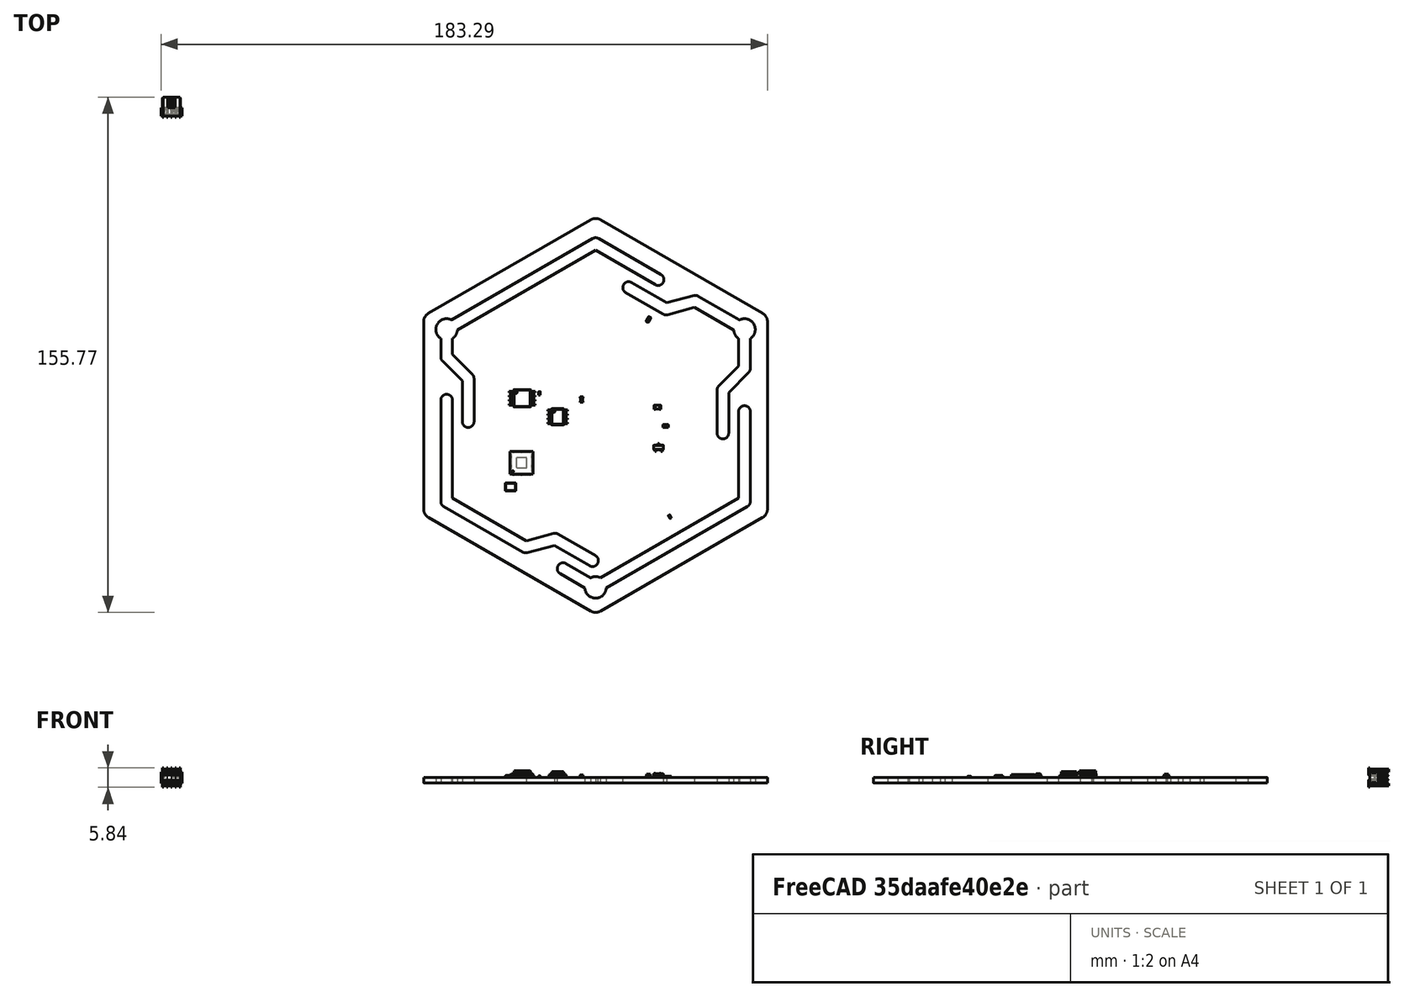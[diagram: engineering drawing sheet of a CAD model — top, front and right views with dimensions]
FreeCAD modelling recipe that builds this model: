
FCSTD DOCUMENT  (FreeCAD 0.21R33771 (Git))
Label: 3d_model
License: All rights reserved
LicenseURL: http://en.wikipedia.org/wiki/All_rights_reserved
objects: App::Link×38, Part::Feature×23, App::Part×5, PartDesign::CoordinateSystem×1, Sketcher::SketchObject×1
note: 25 computed .brp shape members not serialized (recipe doc carries the construction recipe); baked Part::Feature solids carry a one-line shape summary decoded from their .brp

FEATURE [PartDesign::CoordinateSystem] Local_CS_31ac
  AttacherType = Attacher::AttachEngine3D
  MapMode = 2
  Support = -> [X_Axis001]
FEATURE [Part::Feature] Pcb_31ac
  shape: bbox 103.9 x 119.2 x 1.6 mm, 89 faces (baked)
FEATURE [Sketcher::SketchObject] PCB_Sketch_31ac
  FullyConstrained = false
  sketch-geometry (357):
    g0: LineSegment StartX=171.398 StartY=-75.5717 StartZ=0 EndX=171.398 EndY=-67.2627 EndZ=0
    g1: LineSegment StartX=84.9254 StartY=-67.2627 StartZ=0 EndX=84.9254 EndY=-72.117 EndZ=0
    g2: LineSegment StartX=116.846 StartY=-126.377 StartZ=0 EndX=128.134 EndY=-132.894 EndZ=0
    g3: LineSegment StartX=81.3976 StartY=-116.498 StartZ=0 EndX=81.3976 EndY=-85.8817 EndZ=0
    g4: LineSegment StartX=168.408 StartY=-83.55 StartZ=0 EndX=168.408 EndY=-95.8535 EndZ=0
    g5: LineSegment StartX=165.397 StartY=-81.5722 StartZ=0 EndX=171.398 EndY=-75.5717 EndZ=0
    g6: LineSegment StartX=174.925 StartY=-89.3365 StartZ=0 EndX=174.925 EndY=-116.498 EndZ=0
    g7: LineSegment StartX=107.31 StartY=-128.404 StartZ=0 EndX=115.506 EndY=-126.201 EndZ=0
    g8: LineSegment StartX=178.623 StartY=-121.384 StartZ=0 EndX=129.662 EndY=-149.652 EndZ=0
    g9: LineSegment StartX=106.179 StartY=-131.825 StartZ=0 EndX=82.2796 EndY=-118.026 EndZ=0
    g10: LineSegment StartX=129.662 StartY=-31.3837 StartZ=0 EndX=178.623 EndY=-59.6516 EndZ=0
    g11: LineSegment StartX=174.925 StartY=-67.2627 StartZ=0 EndX=174.925 EndY=-76.3024 EndZ=0
    g12: LineSegment StartX=124.916 StartY=-142.642 StartZ=0 EndX=117.467 EndY=-138.342 EndZ=0
    g13: LineSegment StartX=84.6472 StartY=-61.6424 StartZ=0 EndX=127.28 EndY=-37.0286 EndZ=0
    g14: LineSegment StartX=84.9254 StartY=-85.8817 StartZ=0 EndX=84.9254 EndY=-115.48 EndZ=0
    g15: LineSegment StartX=84.9254 StartY=-72.117 StartZ=0 EndX=90.9258 EndY=-78.1174 EndZ=0
    g16: LineSegment StartX=149.694 StartY=-56.4882 StartZ=0 EndX=157.891 EndY=-54.2919 EndZ=0
    g17: LineSegment StartX=139.039 StartY=-50.3365 StartZ=0 EndX=149.694 EndY=-56.4882 EndZ=0
    g18: LineSegment StartX=148.563 StartY=-59.9087 StartZ=0 EndX=137.275 EndY=-53.3916 EndZ=0
    g19: LineSegment StartX=77.6829 StartY=-59.6615 StartZ=0 EndX=126.662 EndY=-31.3837 EndZ=0
    g20: LineSegment StartX=126.37 StartY=-135.949 StartZ=0 EndX=115.715 EndY=-129.798 EndZ=0
    g21: LineSegment StartX=128.161 StartY=-40.5932 StartZ=0 EndX=86.4073 EndY=-64.6997 EndZ=0
    g22: LineSegment StartX=159.229 StartY=-54.4676 StartZ=0 EndX=171.674 EndY=-61.6432 EndZ=0
    g23: LineSegment StartX=81.3976 StartY=-72.8476 StartZ=0 EndX=81.3976 EndY=-67.2627 EndZ=0
    g24: LineSegment StartX=146.177 StartY=-51.0058 StartZ=0 EndX=128.161 EndY=-40.5932 EndZ=0
    g25: LineSegment StartX=171.398 StartY=-115.48 StartZ=0 EndX=171.398 EndY=-89.3365 EndZ=0
    g26: LineSegment StartX=174.043 StartY=-118.026 StartZ=0 EndX=131.408 EndY=-142.642 EndZ=0
    g27: LineSegment StartX=119.231 StartY=-135.286 StartZ=0 EndX=126.679 EndY=-139.587 EndZ=0
    g28: LineSegment StartX=129.644 StartY=-139.587 StartZ=0 EndX=171.398 EndY=-115.48 EndZ=0
    g29: LineSegment StartX=115.715 StartY=-129.798 StartZ=0 EndX=107.519 EndY=-132 EndZ=0
    g30: LineSegment StartX=91.4425 StartY=-79.3646 StartZ=0 EndX=91.4425 EndY=-92.3987 EndZ=0
    g31: LineSegment StartX=76.2 StartY=-118.8 StartZ=0 EndX=76.2 EndY=-62.23 EndZ=0
    g32: LineSegment StartX=84.9254 StartY=-115.48 StartZ=0 EndX=107.31 EndY=-128.404 EndZ=0
    g33: LineSegment StartX=164.881 StartY=-95.8535 StartZ=0 EndX=164.881 EndY=-82.8194 EndZ=0
    g34: LineSegment StartX=129.044 StartY=-37.029 StartZ=0 EndX=147.942 EndY=-47.9515 EndZ=0
    g35: LineSegment StartX=158.099 StartY=-57.8884 StartZ=0 EndX=149.902 EndY=-60.0849 EndZ=0
    g36: LineSegment StartX=169.916 StartY=-64.7016 StartZ=0 EndX=158.099 EndY=-57.8884 EndZ=0
    g37: LineSegment StartX=174.409 StartY=-77.5496 StartZ=0 EndX=168.408 EndY=-83.55 EndZ=0
    g38: LineSegment StartX=87.9147 StartY=-80.0953 StartZ=0 EndX=81.9143 EndY=-74.0949 EndZ=0
    g39: LineSegment StartX=180.123 StartY=-62.2497 StartZ=0 EndX=180.123 EndY=-118.786 EndZ=0
    g40: LineSegment StartX=87.9147 StartY=-92.3987 StartZ=0 EndX=87.9147 EndY=-80.0953 EndZ=0
    g41: LineSegment StartX=126.662 StartY=-149.652 StartZ=0 EndX=77.6877 EndY=-121.377 EndZ=0
    g42: BSplineCurve PolesCount=4 KnotsCount=2 Degree=3 IsPeriodic=0
    g43: BSplineCurve PolesCount=4 KnotsCount=2 Degree=3 IsPeriodic=0
    g44: BSplineCurve PolesCount=4 KnotsCount=2 Degree=3 IsPeriodic=0
    g45: BSplineCurve PolesCount=4 KnotsCount=2 Degree=3 IsPeriodic=0
    g46: BSplineCurve PolesCount=4 KnotsCount=2 Degree=3 IsPeriodic=0
    g47: BSplineCurve PolesCount=4 KnotsCount=2 Degree=3 IsPeriodic=0
    g48: BSplineCurve PolesCount=4 KnotsCount=2 Degree=3 IsPeriodic=0
    g49: BSplineCurve PolesCount=4 KnotsCount=2 Degree=3 IsPeriodic=0
    g50: BSplineCurve PolesCount=4 KnotsCount=2 Degree=3 IsPeriodic=0
    g51: BSplineCurve PolesCount=4 KnotsCount=2 Degree=3 IsPeriodic=0
    g52: BSplineCurve PolesCount=4 KnotsCount=2 Degree=3 IsPeriodic=0
    g53: BSplineCurve PolesCount=4 KnotsCount=2 Degree=3 IsPeriodic=0
    g54: BSplineCurve PolesCount=4 KnotsCount=2 Degree=3 IsPeriodic=0
    g55: BSplineCurve PolesCount=4 KnotsCount=2 Degree=3 IsPeriodic=0
    g56: BSplineCurve PolesCount=4 KnotsCount=2 Degree=3 IsPeriodic=0
    g57: BSplineCurve PolesCount=4 KnotsCount=2 Degree=3 IsPeriodic=0
    g58: BSplineCurve PolesCount=4 KnotsCount=2 Degree=3 IsPeriodic=0
    g59: BSplineCurve PolesCount=4 KnotsCount=2 Degree=3 IsPeriodic=0
    g60: BSplineCurve PolesCount=4 KnotsCount=2 Degree=3 IsPeriodic=0
    g61: BSplineCurve PolesCount=4 KnotsCount=2 Degree=3 IsPeriodic=0
    g62: BSplineCurve PolesCount=4 KnotsCount=2 Degree=3 IsPeriodic=0
    g63: BSplineCurve PolesCount=4 KnotsCount=2 Degree=3 IsPeriodic=0
    g64: BSplineCurve PolesCount=4 KnotsCount=2 Degree=3 IsPeriodic=0
    g65: BSplineCurve PolesCount=4 KnotsCount=2 Degree=3 IsPeriodic=0
    g66: BSplineCurve PolesCount=4 KnotsCount=2 Degree=3 IsPeriodic=0
    g67: BSplineCurve PolesCount=4 KnotsCount=2 Degree=3 IsPeriodic=0
    g68: BSplineCurve PolesCount=4 KnotsCount=2 Degree=3 IsPeriodic=0
    g69: BSplineCurve PolesCount=4 KnotsCount=2 Degree=3 IsPeriodic=0
    g70: BSplineCurve PolesCount=4 KnotsCount=2 Degree=3 IsPeriodic=0
    g71: BSplineCurve PolesCount=4 KnotsCount=2 Degree=3 IsPeriodic=0
    g72: BSplineCurve PolesCount=4 KnotsCount=2 Degree=3 IsPeriodic=0
    g73: BSplineCurve PolesCount=4 KnotsCount=2 Degree=3 IsPeriodic=0
    g74: BSplineCurve PolesCount=4 KnotsCount=2 Degree=3 IsPeriodic=0
    g75: BSplineCurve PolesCount=4 KnotsCount=2 Degree=3 IsPeriodic=0
    g76: BSplineCurve PolesCount=4 KnotsCount=2 Degree=3 IsPeriodic=0
    g77: BSplineCurve PolesCount=4 KnotsCount=2 Degree=3 IsPeriodic=0
    g78: BSplineCurve PolesCount=4 KnotsCount=2 Degree=3 IsPeriodic=0
    g79: BSplineCurve PolesCount=4 KnotsCount=2 Degree=3 IsPeriodic=0
    g80: BSplineCurve PolesCount=4 KnotsCount=2 Degree=3 IsPeriodic=0
    g81: BSplineCurve PolesCount=4 KnotsCount=2 Degree=3 IsPeriodic=0
    g82: BSplineCurve PolesCount=4 KnotsCount=2 Degree=3 IsPeriodic=0
    g83: BSplineCurve PolesCount=4 KnotsCount=2 Degree=3 IsPeriodic=0
    g84: BSplineCurve PolesCount=4 KnotsCount=2 Degree=3 IsPeriodic=0
    g85: BSplineCurve PolesCount=4 KnotsCount=2 Degree=3 IsPeriodic=0
    g86: BSplineCurve PolesCount=4 KnotsCount=2 Degree=3 IsPeriodic=0
    g87-g90: Circle x4 (B-spline internal-alignment scaffolding for g42; pole/knot coordinates omitted)
    g91: GeomPoint X=126.662 Y=-31.3837 Z=0
    g92: GeomPoint X=129.662 Y=-31.3837 Z=0
    g93-g96: Circle x4 (B-spline internal-alignment scaffolding for g43; pole/knot coordinates omitted)
    g97: GeomPoint X=157.891 Y=-54.2919 Z=0
    g98: GeomPoint X=159.229 Y=-54.4676 Z=0
    g99-g102: Circle x4 (B-spline internal-alignment scaffolding for g44; pole/knot coordinates omitted)
    g103: GeomPoint X=147.942 Y=-47.9515 Z=0
    g104: GeomPoint X=148.587 Y=-50.3613 Z=0
    g105-g108: Circle x4 (B-spline internal-alignment scaffolding for g45; pole/knot coordinates omitted)
    g109: GeomPoint X=83.1615 Y=-61.2831 Z=0
    g110: GeomPoint X=84.6472 Y=-61.6424 Z=0
    g111-g114: Circle x4 (B-spline internal-alignment scaffolding for g46; pole/knot coordinates omitted)
    g115: GeomPoint X=81.3976 Y=-67.2627 Z=0
    g116: GeomPoint X=79.9115 Y=-64.5332 Z=0
    g117-g120: Circle x4 (B-spline internal-alignment scaffolding for g47; pole/knot coordinates omitted)
    g121: GeomPoint X=131.408 Y=-142.642 Z=0
    g122: GeomPoint X=128.162 Y=-145.729 Z=0
    g123-g126: Circle x4 (B-spline internal-alignment scaffolding for g48; pole/knot coordinates omitted)
    g127: GeomPoint X=90.9258 Y=-78.1174 Z=0
    g128: GeomPoint X=91.4425 Y=-79.3646 Z=0
    g129-g132: Circle x4 (B-spline internal-alignment scaffolding for g49; pole/knot coordinates omitted)
    g133: GeomPoint X=176.412 Y=-64.5332 Z=0
    g134: GeomPoint X=174.925 Y=-67.2627 Z=0
    g135-g138: Circle x4 (B-spline internal-alignment scaffolding for g50; pole/knot coordinates omitted)
    g139: GeomPoint X=180.123 Y=-118.786 Z=0
    g140: GeomPoint X=178.623 Y=-121.384 Z=0
    g141-g144: Circle x4 (B-spline internal-alignment scaffolding for g51; pole/knot coordinates omitted)
    g145: GeomPoint X=164.881 Y=-82.8194 Z=0
    g146: GeomPoint X=165.397 Y=-81.5722 Z=0
    g147-g150: Circle x4 (B-spline internal-alignment scaffolding for g52; pole/knot coordinates omitted)
    g151: GeomPoint X=117.467 Y=-138.342 Z=0
    g152: GeomPoint X=116.822 Y=-135.932 Z=0
    g153-g156: Circle x4 (B-spline internal-alignment scaffolding for g53; pole/knot coordinates omitted)
    g157: GeomPoint X=81.3976 Y=-85.8817 Z=0
    g158: GeomPoint X=83.1615 Y=-84.1178 Z=0
    g159-g162: Circle x4 (B-spline internal-alignment scaffolding for g54; pole/knot coordinates omitted)
    g163: GeomPoint X=126.679 Y=-139.587 Z=0
    g164: GeomPoint X=128.162 Y=-139.229 Z=0
    g165-g168: Circle x4 (B-spline internal-alignment scaffolding for g55; pole/knot coordinates omitted)
    g169: GeomPoint X=107.519 Y=-132 Z=0
    g170: GeomPoint X=106.179 Y=-131.825 Z=0
    g171-g174: Circle x4 (B-spline internal-alignment scaffolding for g56; pole/knot coordinates omitted)
    g175: GeomPoint X=115.506 Y=-126.201 Z=0
    g176: GeomPoint X=116.846 Y=-126.377 Z=0
    g177-g180: Circle x4 (B-spline internal-alignment scaffolding for g57; pole/knot coordinates omitted)
    g181: GeomPoint X=137.275 Y=-53.3916 Z=0
    g182: GeomPoint X=136.63 Y=-50.9821 Z=0
    g183-g186: Circle x4 (B-spline internal-alignment scaffolding for g58; pole/knot coordinates omitted)
    g187: GeomPoint X=76.2 Y=-62.23 Z=0
    g188: GeomPoint X=77.6829 Y=-59.6615 Z=0
    g189-g192: Circle x4 (B-spline internal-alignment scaffolding for g59; pole/knot coordinates omitted)
    g193: GeomPoint X=128.134 Y=-132.894 Z=0
    g194: GeomPoint X=128.779 Y=-135.303 Z=0
    g195-g198: Circle x4 (B-spline internal-alignment scaffolding for g60; pole/knot coordinates omitted)
    g199: GeomPoint X=136.63 Y=-50.9821 Z=0
    g200: GeomPoint X=139.039 Y=-50.3365 Z=0
    g201-g204: Circle x4 (B-spline internal-alignment scaffolding for g61; pole/knot coordinates omitted)
    g205: GeomPoint X=127.28 Y=-37.0286 Z=0
    g206: GeomPoint X=129.044 Y=-37.029 Z=0
    g207-g210: Circle x4 (B-spline internal-alignment scaffolding for g62; pole/knot coordinates omitted)
    g211: GeomPoint X=128.162 Y=-145.729 Z=0
    g212: GeomPoint X=124.916 Y=-142.642 Z=0
    g213-g216: Circle x4 (B-spline internal-alignment scaffolding for g63; pole/knot coordinates omitted)
    g217: GeomPoint X=79.9115 Y=-64.5332 Z=0
    g218: GeomPoint X=83.1615 Y=-61.2831 Z=0
    g219-g222: Circle x4 (B-spline internal-alignment scaffolding for g64; pole/knot coordinates omitted)
    g223: GeomPoint X=174.925 Y=-116.498 Z=0
    g224: GeomPoint X=174.043 Y=-118.026 Z=0
    g225-g228: Circle x4 (B-spline internal-alignment scaffolding for g65; pole/knot coordinates omitted)
    g229: GeomPoint X=116.822 Y=-135.932 Z=0
    g230: GeomPoint X=119.231 Y=-135.286 Z=0
    g231-g234: Circle x4 (B-spline internal-alignment scaffolding for g66; pole/knot coordinates omitted)
    g235: GeomPoint X=82.2796 Y=-118.026 Z=0
    g236: GeomPoint X=81.3976 Y=-116.498 Z=0
    g237-g240: Circle x4 (B-spline internal-alignment scaffolding for g67; pole/knot coordinates omitted)
    g241: GeomPoint X=168.408 Y=-95.8535 Z=0
    g242: GeomPoint X=166.644 Y=-97.6174 Z=0
    g243-g246: Circle x4 (B-spline internal-alignment scaffolding for g68; pole/knot coordinates omitted)
    g247: GeomPoint X=148.587 Y=-50.3613 Z=0
    g248: GeomPoint X=146.177 Y=-51.0058 Z=0
    g249-g252: Circle x4 (B-spline internal-alignment scaffolding for g69; pole/knot coordinates omitted)
    g253: GeomPoint X=171.674 Y=-61.6432 Z=0
    g254: GeomPoint X=173.162 Y=-61.2831 Z=0
    g255-g258: Circle x4 (B-spline internal-alignment scaffolding for g70; pole/knot coordinates omitted)
    g259: GeomPoint X=128.779 Y=-135.303 Z=0
    g260: GeomPoint X=126.37 Y=-135.949 Z=0
    g261-g264: Circle x4 (B-spline internal-alignment scaffolding for g71; pole/knot coordinates omitted)
    g265: GeomPoint X=81.9143 Y=-74.0949 Z=0
    g266: GeomPoint X=81.3976 Y=-72.8476 Z=0
    g267-g270: Circle x4 (B-spline internal-alignment scaffolding for g72; pole/knot coordinates omitted)
    g271: GeomPoint X=171.398 Y=-89.3365 Z=0
    g272: GeomPoint X=173.162 Y=-87.5726 Z=0
    g273-g276: Circle x4 (B-spline internal-alignment scaffolding for g73; pole/knot coordinates omitted)
    g277: GeomPoint X=129.662 Y=-149.652 Z=0
    g278: GeomPoint X=126.662 Y=-149.652 Z=0
    g279-g282: Circle x4 (B-spline internal-alignment scaffolding for g74; pole/knot coordinates omitted)
    g283: GeomPoint X=77.6877 Y=-121.377 Z=0
    g284: GeomPoint X=76.2 Y=-118.8 Z=0
    g285-g288: Circle x4 (B-spline internal-alignment scaffolding for g75; pole/knot coordinates omitted)
    g289: GeomPoint X=86.4073 Y=-64.6997 Z=0
    g290: GeomPoint X=84.9254 Y=-67.2627 Z=0
    g291-g294: Circle x4 (B-spline internal-alignment scaffolding for g76; pole/knot coordinates omitted)
    g295: GeomPoint X=91.4425 Y=-92.3987 Z=0
    g296: GeomPoint X=89.6786 Y=-94.1626 Z=0
    g297-g300: Circle x4 (B-spline internal-alignment scaffolding for g77; pole/knot coordinates omitted)
    g301: GeomPoint X=171.398 Y=-67.2627 Z=0
    g302: GeomPoint X=169.916 Y=-64.7016 Z=0
    g303-g306: Circle x4 (B-spline internal-alignment scaffolding for g78; pole/knot coordinates omitted)
    g307: GeomPoint X=173.162 Y=-61.2831 Z=0
    g308: GeomPoint X=176.412 Y=-64.5332 Z=0
    g309-g312: Circle x4 (B-spline internal-alignment scaffolding for g79; pole/knot coordinates omitted)
    g313: GeomPoint X=89.6786 Y=-94.1626 Z=0
    g314: GeomPoint X=87.9147 Y=-92.3987 Z=0
    g315-g318: Circle x4 (B-spline internal-alignment scaffolding for g80; pole/knot coordinates omitted)
    g319: GeomPoint X=149.902 Y=-60.0849 Z=0
    g320: GeomPoint X=148.563 Y=-59.9087 Z=0
    g321-g324: Circle x4 (B-spline internal-alignment scaffolding for g81; pole/knot coordinates omitted)
    g325: GeomPoint X=128.162 Y=-139.229 Z=0
    g326: GeomPoint X=129.644 Y=-139.587 Z=0
    g327-g330: Circle x4 (B-spline internal-alignment scaffolding for g82; pole/knot coordinates omitted)
    g331: GeomPoint X=166.644 Y=-97.6174 Z=0
    g332: GeomPoint X=164.881 Y=-95.8535 Z=0
    g333-g336: Circle x4 (B-spline internal-alignment scaffolding for g83; pole/knot coordinates omitted)
    g337: GeomPoint X=178.623 Y=-59.6516 Z=0
    g338: GeomPoint X=180.123 Y=-62.2497 Z=0
    g339-g342: Circle x4 (B-spline internal-alignment scaffolding for g84; pole/knot coordinates omitted)
    g343: GeomPoint X=173.162 Y=-87.5726 Z=0
    g344: GeomPoint X=174.925 Y=-89.3365 Z=0
    g345-g348: Circle x4 (B-spline internal-alignment scaffolding for g85; pole/knot coordinates omitted)
    g349: GeomPoint X=83.1615 Y=-84.1178 Z=0
    g350: GeomPoint X=84.9254 Y=-85.8817 Z=0
    g351-g354: Circle x4 (B-spline internal-alignment scaffolding for g86; pole/knot coordinates omitted)
    g355: GeomPoint X=174.925 Y=-76.3024 Z=0
    g356: GeomPoint X=174.409 Y=-77.5496 Z=0
  constraints (537):
    c: Coincident(g31,g74)
    c: Coincident(g31,g58)
    c: Coincident(g41,g74)
    c: Coincident(g19,g58)
    c: Coincident(g46,g63)
    c: Coincident(g3,g66)
    c: Coincident(g3,g53)
    c: Coincident(g23,g71)
    c: Coincident(g23,g46)
    c: Coincident(g38,g71)
    c: Coincident(g9,g66)
    c: Coincident(g53,g85)
    c: Coincident(g45,g63)
    c: Coincident(g13,g45)
    c: Coincident(g14,g32)
    c: Coincident(g14,g85)
    c: Coincident(g1,g15)
    c: Coincident(g1,g75)
    c: Coincident(g21,g75)
    c: Coincident(g40,g79)
    c: Coincident(g38,g40)
    c: Coincident(g76,g79)
    c: Coincident(g15,g48)
    c: Coincident(g30,g76)
    c: Coincident(g30,g48)
    c: Coincident(g9,g55)
    c: Coincident(g7,g32)
    c: Coincident(g29,g55)
    c: Coincident(g7,g56)
    c: Coincident(g20,g29)
    c: Coincident(g52,g65)
    c: Coincident(g2,g56)
    c: Coincident(g12,g52)
    c: Coincident(g27,g65)
    c: Coincident(g12,g62)
    c: Coincident(g20,g70)
    c: Coincident(g41,g73)
    c: Coincident(g19,g42)
    c: Coincident(g27,g54)
    c: Coincident(g13,g61)
    c: Coincident(g2,g59)
    c: Coincident(g47,g62)
    c: Coincident(g54,g81)
    c: Coincident(g21,g24)
    c: Coincident(g59,g70)
    c: Coincident(g34,g61)
    c: Coincident(g28,g81)
    c: Coincident(g8,g73)
    c: Coincident(g10,g42)
    c: Coincident(g26,g47)
    c: Coincident(g57,g60)
    c: Coincident(g18,g57)
    c: Coincident(g17,g60)
    c: Coincident(g24,g68)
    c: Coincident(g34,g44)
    c: Coincident(g18,g80)
    c: Coincident(g44,g68)
    c: Coincident(g16,g17)
    c: Coincident(g35,g80)
    c: Coincident(g16,g43)
    c: Coincident(g35,g36)
    c: Coincident(g22,g43)
    c: Coincident(g33,g82)
    c: Coincident(g33,g51)
    c: Coincident(g5,g51)
    c: Coincident(g67,g82)
    c: Coincident(g4,g67)
    c: Coincident(g4,g37)
    c: Coincident(g36,g77)
    c: Coincident(g25,g28)
    c: Coincident(g25,g72)
    c: Coincident(g0,g5)
    c: Coincident(g0,g77)
    c: Coincident(g22,g69)
    c: Coincident(g72,g84)
    c: Coincident(g69,g78)
    c: Coincident(g26,g64)
    c: Coincident(g37,g86)
    c: Coincident(g6,g64)
    c: Coincident(g6,g84)
    c: Coincident(g11,g86)
    c: Coincident(g11,g49)
    c: Coincident(g49,g78)
    c: Coincident(g8,g50)
    c: Coincident(g10,g83)
    c: Coincident(g39,g50)
    c: Coincident(g39,g83)
    c: InternalAlignment(g87,g42)
    c: Weight(g87) = 1
    c: InternalAlignment(g88,g42)
    c: Equal(g88,g87)
    c: InternalAlignment(g89,g42)
    c: Equal(g89,g87)
    c: InternalAlignment(g90,g42)
    c: Equal(g90,g87)
    c: InternalAlignment(g91,g42)
    c: InternalAlignment(g92,g42)
    c: InternalAlignment(g93,g43)
    c: Weight(g93) = 1
    c: InternalAlignment(g94,g43)
    c: Equal(g94,g93)
    c: InternalAlignment(g95,g43)
    c: Equal(g95,g93)
    c: InternalAlignment(g96,g43)
    c: Equal(g96,g93)
    c: InternalAlignment(g97,g43)
    c: InternalAlignment(g98,g43)
    c: InternalAlignment(g99,g44)
    c: Weight(g99) = 1
    c: InternalAlignment(g100,g44)
    c: Equal(g100,g99)
    c: InternalAlignment(g101,g44)
    c: Equal(g101,g99)
    c: InternalAlignment(g102,g44)
    c: Equal(g102,g99)
    c: InternalAlignment(g103,g44)
    c: InternalAlignment(g104,g44)
    c: InternalAlignment(g105,g45)
    c: Weight(g105) = 1
    c: InternalAlignment(g106,g45)
    c: Equal(g106,g105)
    c: InternalAlignment(g107,g45)
    c: Equal(g107,g105)
    c: InternalAlignment(g108,g45)
    c: Equal(g108,g105)
    c: InternalAlignment(g109,g45)
    c: InternalAlignment(g110,g45)
    c: InternalAlignment(g111,g46)
    c: Weight(g111) = 1
    c: InternalAlignment(g112,g46)
    c: Equal(g112,g111)
    c: InternalAlignment(g113,g46)
    c: Equal(g113,g111)
    c: InternalAlignment(g114,g46)
    c: Equal(g114,g111)
    c: InternalAlignment(g115,g46)
    c: InternalAlignment(g116,g46)
    c: InternalAlignment(g117,g47)
    c: Weight(g117) = 1
    c: InternalAlignment(g118,g47)
    c: Equal(g118,g117)
    c: InternalAlignment(g119,g47)
    c: Equal(g119,g117)
    c: InternalAlignment(g120,g47)
    c: Equal(g120,g117)
    c: InternalAlignment(g121,g47)
    c: InternalAlignment(g122,g47)
    c: InternalAlignment(g123,g48)
    c: Weight(g123) = 1
    c: InternalAlignment(g124,g48)
    c: Equal(g124,g123)
    c: InternalAlignment(g125,g48)
    c: Equal(g125,g123)
    c: InternalAlignment(g126,g48)
    c: Equal(g126,g123)
    c: InternalAlignment(g127,g48)
    c: InternalAlignment(g128,g48)
    c: InternalAlignment(g129,g49)
    c: Weight(g129) = 1
    c: InternalAlignment(g130,g49)
    c: Equal(g130,g129)
    c: InternalAlignment(g131,g49)
    c: Equal(g131,g129)
    c: InternalAlignment(g132,g49)
    c: Equal(g132,g129)
    c: InternalAlignment(g133,g49)
    c: InternalAlignment(g134,g49)
    c: InternalAlignment(g135,g50)
    c: Weight(g135) = 1
    c: InternalAlignment(g136,g50)
    c: Equal(g136,g135)
    c: InternalAlignment(g137,g50)
    c: Equal(g137,g135)
    c: InternalAlignment(g138,g50)
    c: Equal(g138,g135)
    c: InternalAlignment(g139,g50)
    c: InternalAlignment(g140,g50)
    c: InternalAlignment(g141,g51)
    c: Weight(g141) = 1
    c: InternalAlignment(g142,g51)
    c: Equal(g142,g141)
    c: InternalAlignment(g143,g51)
    c: Equal(g143,g141)
    c: InternalAlignment(g144,g51)
    c: Equal(g144,g141)
    c: InternalAlignment(g145,g51)
    c: InternalAlignment(g146,g51)
    c: InternalAlignment(g147,g52)
    c: Weight(g147) = 1
    c: InternalAlignment(g148,g52)
    c: Equal(g148,g147)
    c: InternalAlignment(g149,g52)
    c: Equal(g149,g147)
    c: InternalAlignment(g150,g52)
    c: Equal(g150,g147)
    c: InternalAlignment(g151,g52)
    c: InternalAlignment(g152,g52)
    c: InternalAlignment(g153,g53)
    c: Weight(g153) = 1
    c: InternalAlignment(g154,g53)
    c: Equal(g154,g153)
    c: InternalAlignment(g155,g53)
    c: Equal(g155,g153)
    c: InternalAlignment(g156,g53)
    c: Equal(g156,g153)
    c: InternalAlignment(g157,g53)
    c: InternalAlignment(g158,g53)
    c: InternalAlignment(g159,g54)
    c: Weight(g159) = 1
    c: InternalAlignment(g160,g54)
    c: Equal(g160,g159)
    c: InternalAlignment(g161,g54)
    c: Equal(g161,g159)
    c: InternalAlignment(g162,g54)
    c: Equal(g162,g159)
    c: InternalAlignment(g163,g54)
    c: InternalAlignment(g164,g54)
    c: InternalAlignment(g165,g55)
    c: Weight(g165) = 1
    c: InternalAlignment(g166,g55)
    c: Equal(g166,g165)
    c: InternalAlignment(g167,g55)
    c: Equal(g167,g165)
    c: InternalAlignment(g168,g55)
    c: Equal(g168,g165)
    c: InternalAlignment(g169,g55)
    c: InternalAlignment(g170,g55)
    c: InternalAlignment(g171,g56)
    c: Weight(g171) = 1
    c: InternalAlignment(g172,g56)
    c: Equal(g172,g171)
    c: InternalAlignment(g173,g56)
    c: Equal(g173,g171)
    c: InternalAlignment(g174,g56)
    c: Equal(g174,g171)
    c: InternalAlignment(g175,g56)
    c: InternalAlignment(g176,g56)
    c: InternalAlignment(g177,g57)
    c: Weight(g177) = 1
    c: InternalAlignment(g178,g57)
    c: Equal(g178,g177)
    c: InternalAlignment(g179,g57)
    c: Equal(g179,g177)
    c: InternalAlignment(g180,g57)
    c: Equal(g180,g177)
    c: InternalAlignment(g181,g57)
    c: InternalAlignment(g182,g57)
    c: InternalAlignment(g183,g58)
    c: Weight(g183) = 1
    c: InternalAlignment(g184,g58)
    c: Equal(g184,g183)
    c: InternalAlignment(g185,g58)
    c: Equal(g185,g183)
    c: InternalAlignment(g186,g58)
    c: Equal(g186,g183)
    c: InternalAlignment(g187,g58)
    c: InternalAlignment(g188,g58)
    c: InternalAlignment(g189,g59)
    c: Weight(g189) = 1
    c: InternalAlignment(g190,g59)
    c: Equal(g190,g189)
    c: InternalAlignment(g191,g59)
    c: Equal(g191,g189)
    c: InternalAlignment(g192,g59)
    c: Equal(g192,g189)
    c: InternalAlignment(g193,g59)
    c: InternalAlignment(g194,g59)
    c: InternalAlignment(g195,g60)
    c: Weight(g195) = 1
    c: InternalAlignment(g196,g60)
    c: Equal(g196,g195)
    c: InternalAlignment(g197,g60)
    c: Equal(g197,g195)
    c: InternalAlignment(g198,g60)
    c: Equal(g198,g195)
    c: InternalAlignment(g199,g60)
    c: InternalAlignment(g200,g60)
    c: InternalAlignment(g201,g61)
    c: Weight(g201) = 1
    c: InternalAlignment(g202,g61)
    c: Equal(g202,g201)
    c: InternalAlignment(g203,g61)
    c: Equal(g203,g201)
    c: InternalAlignment(g204,g61)
    c: Equal(g204,g201)
    c: InternalAlignment(g205,g61)
    c: InternalAlignment(g206,g61)
    c: InternalAlignment(g207,g62)
    c: Weight(g207) = 1
    c: InternalAlignment(g208,g62)
    c: Equal(g208,g207)
    c: InternalAlignment(g209,g62)
    c: Equal(g209,g207)
    c: InternalAlignment(g210,g62)
    c: Equal(g210,g207)
    c: InternalAlignment(g211,g62)
    c: InternalAlignment(g212,g62)
    c: InternalAlignment(g213,g63)
    c: Weight(g213) = 1
    c: InternalAlignment(g214,g63)
    c: Equal(g214,g213)
    c: InternalAlignment(g215,g63)
    c: Equal(g215,g213)
    c: InternalAlignment(g216,g63)
    c: Equal(g216,g213)
    c: InternalAlignment(g217,g63)
    c: InternalAlignment(g218,g63)
    c: InternalAlignment(g219,g64)
    c: Weight(g219) = 1
    c: InternalAlignment(g220,g64)
    c: Equal(g220,g219)
    c: InternalAlignment(g221,g64)
    c: Equal(g221,g219)
    c: InternalAlignment(g222,g64)
    c: Equal(g222,g219)
    c: InternalAlignment(g223,g64)
    c: InternalAlignment(g224,g64)
    c: InternalAlignment(g225,g65)
    c: Weight(g225) = 1
    c: InternalAlignment(g226,g65)
    c: Equal(g226,g225)
    c: InternalAlignment(g227,g65)
    c: Equal(g227,g225)
    c: InternalAlignment(g228,g65)
    c: Equal(g228,g225)
    c: InternalAlignment(g229,g65)
    c: InternalAlignment(g230,g65)
    c: InternalAlignment(g231,g66)
    c: Weight(g231) = 1
    c: InternalAlignment(g232,g66)
    c: Equal(g232,g231)
    c: InternalAlignment(g233,g66)
    c: Equal(g233,g231)
    c: InternalAlignment(g234,g66)
    c: Equal(g234,g231)
    c: InternalAlignment(g235,g66)
    c: InternalAlignment(g236,g66)
    c: InternalAlignment(g237,g67)
    c: Weight(g237) = 1
    c: InternalAlignment(g238,g67)
    c: Equal(g238,g237)
    c: InternalAlignment(g239,g67)
    c: Equal(g239,g237)
    c: InternalAlignment(g240,g67)
    c: Equal(g240,g237)
    c: InternalAlignment(g241,g67)
    c: InternalAlignment(g242,g67)
    c: InternalAlignment(g243,g68)
    c: Weight(g243) = 1
    c: InternalAlignment(g244,g68)
    c: Equal(g244,g243)
    c: InternalAlignment(g245,g68)
    c: Equal(g245,g243)
    c: InternalAlignment(g246,g68)
    c: Equal(g246,g243)
    c: InternalAlignment(g247,g68)
    c: InternalAlignment(g248,g68)
    c: InternalAlignment(g249,g69)
    c: Weight(g249) = 1
    c: InternalAlignment(g250,g69)
    c: Equal(g250,g249)
    c: InternalAlignment(g251,g69)
    c: Equal(g251,g249)
    c: InternalAlignment(g252,g69)
    c: Equal(g252,g249)
    c: InternalAlignment(g253,g69)
    c: InternalAlignment(g254,g69)
    c: InternalAlignment(g255,g70)
    c: Weight(g255) = 1
    c: InternalAlignment(g256,g70)
    c: Equal(g256,g255)
    c: InternalAlignment(g257,g70)
    c: Equal(g257,g255)
    c: InternalAlignment(g258,g70)
    c: Equal(g258,g255)
    c: InternalAlignment(g259,g70)
    c: InternalAlignment(g260,g70)
    c: InternalAlignment(g261,g71)
    c: Weight(g261) = 1
    c: InternalAlignment(g262,g71)
    c: Equal(g262,g261)
    c: InternalAlignment(g263,g71)
    c: Equal(g263,g261)
    c: InternalAlignment(g264,g71)
    c: Equal(g264,g261)
    c: InternalAlignment(g265,g71)
    c: InternalAlignment(g266,g71)
    c: InternalAlignment(g267,g72)
    c: Weight(g267) = 1
    c: InternalAlignment(g268,g72)
    c: Equal(g268,g267)
    c: InternalAlignment(g269,g72)
    c: Equal(g269,g267)
    c: InternalAlignment(g270,g72)
    c: Equal(g270,g267)
    c: InternalAlignment(g271,g72)
    c: InternalAlignment(g272,g72)
    c: InternalAlignment(g273,g73)
    c: Weight(g273) = 1
    c: InternalAlignment(g274,g73)
    c: Equal(g274,g273)
    c: InternalAlignment(g275,g73)
    c: Equal(g275,g273)
    c: InternalAlignment(g276,g73)
    c: Equal(g276,g273)
    c: InternalAlignment(g277,g73)
    c: InternalAlignment(g278,g73)
    c: InternalAlignment(g279,g74)
    c: Weight(g279) = 1
    c: InternalAlignment(g280,g74)
    c: Equal(g280,g279)
    c: InternalAlignment(g281,g74)
    c: Equal(g281,g279)
    c: InternalAlignment(g282,g74)
    c: Equal(g282,g279)
    c: InternalAlignment(g283,g74)
    c: InternalAlignment(g284,g74)
    c: InternalAlignment(g285,g75)
    c: Weight(g285) = 1
    c: InternalAlignment(g286,g75)
    c: Equal(g286,g285)
    c: InternalAlignment(g287,g75)
    c: Equal(g287,g285)
    c: InternalAlignment(g288,g75)
    c: Equal(g288,g285)
    c: InternalAlignment(g289,g75)
    c: InternalAlignment(g290,g75)
    c: InternalAlignment(g291,g76)
    c: Weight(g291) = 1
    c: InternalAlignment(g292,g76)
    c: Equal(g292,g291)
    c: InternalAlignment(g293,g76)
    c: Equal(g293,g291)
    c: InternalAlignment(g294,g76)
    c: Equal(g294,g291)
    c: InternalAlignment(g295,g76)
    c: InternalAlignment(g296,g76)
    c: InternalAlignment(g297,g77)
    c: Weight(g297) = 1
    c: InternalAlignment(g298,g77)
    c: Equal(g298,g297)
    c: InternalAlignment(g299,g77)
    c: Equal(g299,g297)
    c: InternalAlignment(g300,g77)
    c: Equal(g300,g297)
    c: InternalAlignment(g301,g77)
    c: InternalAlignment(g302,g77)
    c: InternalAlignment(g303,g78)
    c: Weight(g303) = 1
    c: InternalAlignment(g304,g78)
    c: Equal(g304,g303)
    c: InternalAlignment(g305,g78)
    c: Equal(g305,g303)
    c: InternalAlignment(g306,g78)
    c: Equal(g306,g303)
    c: InternalAlignment(g307,g78)
    c: InternalAlignment(g308,g78)
    c: InternalAlignment(g309,g79)
    c: Weight(g309) = 1
    c: InternalAlignment(g310,g79)
    c: Equal(g310,g309)
    c: InternalAlignment(g311,g79)
    c: Equal(g311,g309)
    c: InternalAlignment(g312,g79)
    c: Equal(g312,g309)
    c: InternalAlignment(g313,g79)
    c: InternalAlignment(g314,g79)
    c: InternalAlignment(g315,g80)
    c: Weight(g315) = 1
    c: InternalAlignment(g316,g80)
    c: Equal(g316,g315)
    c: InternalAlignment(g317,g80)
    c: Equal(g317,g315)
    c: InternalAlignment(g318,g80)
    c: Equal(g318,g315)
    c: InternalAlignment(g319,g80)
    c: InternalAlignment(g320,g80)
    c: InternalAlignment(g321,g81)
    c: Weight(g321) = 1
    c: InternalAlignment(g322,g81)
    c: Equal(g322,g321)
    c: InternalAlignment(g323,g81)
    c: Equal(g323,g321)
    c: InternalAlignment(g324,g81)
    c: Equal(g324,g321)
    c: InternalAlignment(g325,g81)
    c: InternalAlignment(g326,g81)
    c: InternalAlignment(g327,g82)
    c: Weight(g327) = 1
    c: InternalAlignment(g328,g82)
    c: Equal(g328,g327)
    c: InternalAlignment(g329,g82)
    c: Equal(g329,g327)
    c: InternalAlignment(g330,g82)
    c: Equal(g330,g327)
    c: InternalAlignment(g331,g82)
    c: InternalAlignment(g332,g82)
    c: InternalAlignment(g333,g83)
    c: Weight(g333) = 1
    c: InternalAlignment(g334,g83)
    c: Equal(g334,g333)
    c: InternalAlignment(g335,g83)
    c: Equal(g335,g333)
    c: InternalAlignment(g336,g83)
    c: Equal(g336,g333)
    c: InternalAlignment(g337,g83)
    c: InternalAlignment(g338,g83)
    c: InternalAlignment(g339,g84)
    c: Weight(g339) = 1
    c: InternalAlignment(g340,g84)
    c: Equal(g340,g339)
    c: InternalAlignment(g341,g84)
    c: Equal(g341,g339)
    c: InternalAlignment(g342,g84)
    c: Equal(g342,g339)
    c: InternalAlignment(g343,g84)
    c: InternalAlignment(g344,g84)
    c: InternalAlignment(g345,g85)
    c: Weight(g345) = 1
    c: InternalAlignment(g346,g85)
    c: Equal(g346,g345)
    c: InternalAlignment(g347,g85)
    c: Equal(g347,g345)
    c: InternalAlignment(g348,g85)
    c: Equal(g348,g345)
    c: InternalAlignment(g349,g85)
    c: InternalAlignment(g350,g85)
    c: InternalAlignment(g351,g86)
    c: Weight(g351) = 1
    c: InternalAlignment(g352,g86)
    c: Equal(g352,g351)
    c: InternalAlignment(g353,g86)
    c: Equal(g353,g351)
    c: InternalAlignment(g354,g86)
    c: Equal(g354,g351)
    c: InternalAlignment(g355,g86)
    c: InternalAlignment(g356,g86)
FEATURE [Part::Feature] Shape  label="${REFERENCE}_C_0402_1005Metric_null"
  Placement = pos=(111.208,-83.82,0) rot=(0,0,-1;1.5708rad)
  shape: bbox 0.5 x 1 x 0.5 mm, 28 faces (baked)
FEATURE [Part::Feature] Shape001  label="${REFERENCE}_QFN_56_1EP_7x7mm_P04mm_EP32x32mm_null"
  Placement = pos=(105.782,-104.835,0) rot=(0,0,1;0rad)
  shape: bbox 7 x 7 x 0.95 mm, 350 faces (baked)
FEATURE [Part::Feature] Shape002  label="${REFERENCE}_R_0603_1608Metric_null"
  Placement = pos=(149.352,-93.726,0) rot=(0,0,1;0rad)
  shape: bbox 1.6 x 0.8 x 0.45 mm, 26 faces (baked)
FEATURE [App::Link] __REFERENCE__R_0603_1608Metric_null_ln_  label="${REFERENCE}_R_0603_1608Metric_null001"
  LinkPlacement = pos=(121.285,-93.853,0) rot=(0,0,1;1.5708rad)
  LinkedObject = -> Shape002
  Placement = pos=(121.285,-93.853,0) rot=(0,0,1;1.5708rad)
FEATURE [Part::Feature] Shape003  label="${REFERENCE}_R_0402_1005Metric_null"
  Placement = pos=(150.575,-121.096,0) rot=(0,0,-1;1.0472rad)
  shape: bbox 0.933 x 1.116 x 0.35 mm, 26 faces (baked)
FEATURE [App::Link] __REFERENCE__C_0402_1005Metric_null_ln_  label="${REFERENCE}_C_0402_1005Metric_null001"
  LinkPlacement = pos=(111.125,-102.235,0) rot=(0,0,1;0rad)
  LinkedObject = -> Shape
  Placement = pos=(111.125,-102.235,0) rot=(0,0,1;0rad)
FEATURE [App::Link] __REFERENCE__R_0402_1005Metric_null_ln_  label="${REFERENCE}_R_0402_1005Metric_null001"
  LinkPlacement = pos=(141.249,-62.751,0) rot=(0,0,1;1.0472rad)
  LinkedObject = -> Shape003
  Placement = pos=(141.249,-62.751,0) rot=(0,0,1;1.0472rad)
FEATURE [App::Link] __REFERENCE__R_0402_1005Metric_null_ln_001  label="${REFERENCE}_R_0402_1005Metric_null002"
  LinkPlacement = pos=(145.796,-96.52,0) rot=(0,0,-1;1.5708rad)
  LinkedObject = -> Shape003
  Placement = pos=(145.796,-96.52,0) rot=(0,0,-1;1.5708rad)
FEATURE [Part::Feature] Shape004  label="${REFERENCE}_C_0805_2012Metric_null"
  Placement = pos=(146.877,-88.011,0) rot=(0,0,1;0rad)
  shape: bbox 2 x 1.25 x 1.25 mm, 28 faces (baked)
FEATURE [App::Link] __REFERENCE__R_0402_1005Metric_null_ln_002  label="${REFERENCE}_R_0402_1005Metric_null003"
  LinkPlacement = pos=(142.898,-63.7035,0) rot=(0,0,1;1.0472rad)
  LinkedObject = -> Shape003
  Placement = pos=(142.898,-63.7035,0) rot=(0,0,1;1.0472rad)
FEATURE [App::Link] __REFERENCE__C_0402_1005Metric_null_ln_001  label="${REFERENCE}_C_0402_1005Metric_null002"
  LinkPlacement = pos=(112.268,-105.918,0) rot=(0,0,1;0rad)
  LinkedObject = -> Shape
  Placement = pos=(112.268,-105.918,0) rot=(0,0,1;0rad)
FEATURE [App::Link] __REFERENCE__R_0402_1005Metric_null_ln_003  label="${REFERENCE}_R_0402_1005Metric_null004"
  LinkPlacement = pos=(149.035,-121.985,0) rot=(0,0,-1;1.0472rad)
  LinkedObject = -> Shape003
  Placement = pos=(149.035,-121.985,0) rot=(0,0,-1;1.0472rad)
FEATURE [Part::Feature] Shape005  label="${REFERENCE}_LED_0603_1608Metric_null"
  Placement = pos=(144.168,-61.5038,0) rot=(0,0,-1;2.0944rad)
  shape: bbox 1.493 x 1.786 x 1.1 mm, 50 faces (baked)
FEATURE [App::Link] __REFERENCE__C_0402_1005Metric_null_ln_002  label="${REFERENCE}_C_0402_1005Metric_null003"
  LinkPlacement = pos=(107.061,-110.109,0) rot=(0,0,-1;1.5708rad)
  LinkedObject = -> Shape
  Placement = pos=(107.061,-110.109,0) rot=(0,0,-1;1.5708rad)
FEATURE [Part::Feature] Shape006  label="${REFERENCE}_C_0603_1608Metric_null"
  Placement = pos=(123.952,-85.725,0) rot=(0,0,-1;1.5708rad)
  shape: bbox 0.8 x 1.6 x 0.8 mm, 28 faces (baked)
FEATURE [App::Link] __REFERENCE__R_0402_1005Metric_null_ln_004  label="${REFERENCE}_R_0402_1005Metric_null005"
  LinkPlacement = pos=(139.599,-61.7985,0) rot=(0,0,1;1.0472rad)
  LinkedObject = -> Shape003
  Placement = pos=(139.599,-61.7985,0) rot=(0,0,1;1.0472rad)
FEATURE [App::Link] __REFERENCE__C_0603_1608Metric_null_ln_  label="${REFERENCE}_C_0603_1608Metric_null001"
  LinkPlacement = pos=(109.347,-98.425,0) rot=(0,0,1;1.5708rad)
  LinkedObject = -> Shape006
  Placement = pos=(109.347,-98.425,0) rot=(0,0,1;1.5708rad)
FEATURE [App::Link] __REFERENCE__C_0402_1005Metric_null_ln_003  label="${REFERENCE}_C_0402_1005Metric_null004"
  LinkPlacement = pos=(121.031,-89.535,0) rot=(0,0,-1;1.5708rad)
  LinkedObject = -> Shape
  Placement = pos=(121.031,-89.535,0) rot=(0,0,-1;1.5708rad)
FEATURE [App::Link] __REFERENCE__C_0402_1005Metric_null_ln_004  label="${REFERENCE}_C_0402_1005Metric_null005"
  LinkPlacement = pos=(105.537,-99.441,0) rot=(0,0,1;1.5708rad)
  LinkedObject = -> Shape
  Placement = pos=(105.537,-99.441,0) rot=(0,0,1;1.5708rad)
FEATURE [App::Link] __REFERENCE__R_0402_1005Metric_null_ln_005  label="${REFERENCE}_R_0402_1005Metric_null006"
  LinkPlacement = pos=(96.901,-91.186,0) rot=(0,0,1;3.14159rad)
  LinkedObject = -> Shape003
  Placement = pos=(96.901,-91.186,0) rot=(0,0,1;3.14159rad)
FEATURE [App::Link] __REFERENCE__R_0402_1005Metric_null_ln_006  label="${REFERENCE}_R_0402_1005Metric_null007"
  LinkPlacement = pos=(96.901,-89.408,0) rot=(0,0,1;3.14159rad)
  LinkedObject = -> Shape003
  Placement = pos=(96.901,-89.408,0) rot=(0,0,1;3.14159rad)
FEATURE [App::Link] __REFERENCE__C_0805_2012Metric_null_ln_  label="${REFERENCE}_C_0805_2012Metric_null001"
  LinkPlacement = pos=(148.844,-96.393,0) rot=(0,0,-1;1.5708rad)
  LinkedObject = -> Shape004
  Placement = pos=(148.844,-96.393,0) rot=(0,0,-1;1.5708rad)
FEATURE [Part::Feature] Shape007  label="${REFERENCE}_Crystal_SMD_3225-4Pin_3.2x2.5mm_null"
  Placement = pos=(102.489,-112.141,0) rot=(0,0,1;3.14159rad)
  shape: bbox 3.2 x 2.501 x 0.64 mm, 28 faces (baked)
FEATURE [Part::Feature] Shape008  label="${REFERENCE}_SOIC_8_39x49mm_P127mm_null"
  Placement = pos=(116.711,-90.927,0) rot=(0,0,1;0rad)
  shape: bbox 6 x 4.9 x 1.75 mm, 156 faces (baked)
FEATURE [App::Link] __REFERENCE__C_0603_1608Metric_null_ln_001  label="${REFERENCE}_C_0603_1608Metric_null002"
  LinkPlacement = pos=(107.823,-98.425,0) rot=(0,0,1;1.5708rad)
  LinkedObject = -> Shape006
  Placement = pos=(107.823,-98.425,0) rot=(0,0,1;1.5708rad)
FEATURE [App::Link] __REFERENCE__R_0603_1608Metric_null_ln_001  label="${REFERENCE}_R_0603_1608Metric_null002"
  LinkPlacement = pos=(147.1,-96.49,0) rot=(0,0,-1;1.5708rad)
  LinkedObject = -> Shape002
  Placement = pos=(147.1,-96.49,0) rot=(0,0,-1;1.5708rad)
FEATURE [App::Link] __REFERENCE__R_0603_1608Metric_null_ln_002  label="${REFERENCE}_R_0603_1608Metric_null003"
  LinkPlacement = pos=(146.304,-93.726,0) rot=(0,0,1;0rad)
  LinkedObject = -> Shape002
  Placement = pos=(146.304,-93.726,0) rot=(0,0,1;0rad)
FEATURE [App::Link] __REFERENCE__LED_0603_1608Metric_null_ln_  label="${REFERENCE}_LED_0603_1608Metric_null001"
  LinkPlacement = pos=(94.361,-91.186,0) rot=(0,0,1;0rad)
  LinkedObject = -> Shape005
  Placement = pos=(94.361,-91.186,0) rot=(0,0,1;0rad)
FEATURE [App::Link] __REFERENCE__LED_0603_1608Metric_null_ln_001  label="${REFERENCE}_LED_0603_1608Metric_null002"
  LinkPlacement = pos=(140.869,-59.5988,0) rot=(0,0,-1;2.0944rad)
  LinkedObject = -> Shape005
  Placement = pos=(140.869,-59.5988,0) rot=(0,0,-1;2.0944rad)
FEATURE [App::Link] __REFERENCE__C_0402_1005Metric_null_ln_005  label="${REFERENCE}_C_0402_1005Metric_null006"
  LinkPlacement = pos=(106.553,-99.441,0) rot=(0,0,1;1.5708rad)
  LinkedObject = -> Shape
  Placement = pos=(106.553,-99.441,0) rot=(0,0,1;1.5708rad)
FEATURE [Part::Feature] Shape009  label="${REFERENCE}_SOIC_8_5275x5275mm_P127mm_null"
  Placement = pos=(106.001,-85.344,0) rot=(0,0,1;0rad)
  shape: bbox 7.9 x 5.275 x 2.055 mm, 156 faces (baked)
FEATURE [App::Link] __REFERENCE__R_0402_1005Metric_null_ln_007  label="${REFERENCE}_R_0402_1005Metric_null008"
  LinkPlacement = pos=(147.495,-122.874,0) rot=(0,0,-1;1.0472rad)
  LinkedObject = -> Shape003
  Placement = pos=(147.495,-122.874,0) rot=(0,0,-1;1.0472rad)
FEATURE [Part::Feature] Shape010  label="${REFERENCE}_SOT_23_null"
  Placement = pos=(147.193,-100.203,0) rot=(0,0,1;1.5708rad)
  shape: bbox 3 x 2.5 x 1.2 mm, 76 faces (baked)
FEATURE [App::Link] __REFERENCE__C_0402_1005Metric_null_ln_006  label="${REFERENCE}_C_0402_1005Metric_null007"
  LinkPlacement = pos=(99.822,-112.141,0) rot=(0,0,1;1.5708rad)
  LinkedObject = -> Shape
  Placement = pos=(99.822,-112.141,0) rot=(0,0,1;1.5708rad)
FEATURE [Part::Feature] Part__Feature  label="FTSH-105-01-L-DV-K_pins2"
  shape: bbox 5.486 x 2.017 x 5.842 mm, 71 faces (baked)
FEATURE [Part::Feature] Part__Feature001  label="FTSH-105-01-L-DV-K_pins1"
  shape: bbox 5.486 x 4.293 x 1.676 mm, 91 faces (baked)
FEATURE [Part::Feature] Part__Feature002  label="FTSH-105-01-L-DV-K_body"
  shape: bbox 6.35 x 5.715 x 5.08 mm, 90 faces (baked)
FEATURE [App::Part] FTSH_105_01_L_DV_K  label="${REFERENCE}_FTSH-105-01-L-DV-K_null"
  Group = -> [Part__Feature,Part__Feature001,Part__Feature002]
  Origin = -> Origin008
  Placement = pos=(118.745,-106.68,0.4) rot=(0.57735,-0.57735,-0.57735;2.0944rad)
FEATURE [App::Link] __REFERENCE__LED_0603_1608Metric_null_ln_002  label="${REFERENCE}_LED_0603_1608Metric_null003"
  LinkPlacement = pos=(94.361,-92.964,0) rot=(0,0,1;0rad)
  LinkedObject = -> Shape005
  Placement = pos=(94.361,-92.964,0) rot=(0,0,1;0rad)
FEATURE [App::Link] __REFERENCE__LED_0603_1608Metric_null_ln_003  label="${REFERENCE}_LED_0603_1608Metric_null004"
  LinkPlacement = pos=(148.765,-125.073,0) rot=(0,0,1;2.0944rad)
  LinkedObject = -> Shape005
  Placement = pos=(148.765,-125.073,0) rot=(0,0,1;2.0944rad)
FEATURE [App::Link] __REFERENCE__C_0402_1005Metric_null_ln_007  label="${REFERENCE}_C_0402_1005Metric_null008"
  LinkPlacement = pos=(100.457,-105.918,0) rot=(0,0,1;3.14159rad)
  LinkedObject = -> Shape
  Placement = pos=(100.457,-105.918,0) rot=(0,0,1;3.14159rad)
FEATURE [App::Link] __REFERENCE__R_0402_1005Metric_null_ln_008  label="${REFERENCE}_R_0402_1005Metric_null009"
  LinkPlacement = pos=(143.702,-89.281,0) rot=(0,0,1;1.5708rad)
  LinkedObject = -> Shape003
  Placement = pos=(143.702,-89.281,0) rot=(0,0,1;1.5708rad)
FEATURE [App::Link] __REFERENCE__C_0402_1005Metric_null_ln_008  label="${REFERENCE}_C_0402_1005Metric_null009"
  LinkPlacement = pos=(110.617,-99.441,0) rot=(0,0,1;1.5708rad)
  LinkedObject = -> Shape
  Placement = pos=(110.617,-99.441,0) rot=(0,0,1;1.5708rad)
FEATURE [App::Link] __REFERENCE__R_0402_1005Metric_null_ln_009  label="${REFERENCE}_R_0402_1005Metric_null010"
  LinkPlacement = pos=(96.901,-92.964,0) rot=(0,0,1;3.14159rad)
  LinkedObject = -> Shape003
  Placement = pos=(96.901,-92.964,0) rot=(0,0,1;3.14159rad)
FEATURE [App::Link] __REFERENCE__LED_0603_1608Metric_null_ln_004  label="${REFERENCE}_LED_0603_1608Metric_null005"
  LinkPlacement = pos=(150.305,-124.184,0) rot=(0,0,1;2.0944rad)
  LinkedObject = -> Shape005
  Placement = pos=(150.305,-124.184,0) rot=(0,0,1;2.0944rad)
FEATURE [App::Link] __REFERENCE__LED_0603_1608Metric_null_ln_005  label="${REFERENCE}_LED_0603_1608Metric_null006"
  LinkPlacement = pos=(151.845,-123.295,0) rot=(0,0,1;2.0944rad)
  LinkedObject = -> Shape005
  Placement = pos=(151.845,-123.295,0) rot=(0,0,1;2.0944rad)
FEATURE [App::Link] __REFERENCE__C_0402_1005Metric_null_ln_009  label="${REFERENCE}_C_0402_1005Metric_null010"
  LinkPlacement = pos=(100.457,-102.235,0) rot=(0,0,1;3.14159rad)
  LinkedObject = -> Shape
  Placement = pos=(100.457,-102.235,0) rot=(0,0,1;3.14159rad)
FEATURE [App::Link] __REFERENCE__LED_0603_1608Metric_null_ln_006  label="${REFERENCE}_LED_0603_1608Metric_null007"
  LinkPlacement = pos=(142.519,-60.5513,0) rot=(0,0,-1;2.0944rad)
  LinkedObject = -> Shape005
  Placement = pos=(142.519,-60.5513,0) rot=(0,0,-1;2.0944rad)
FEATURE [App::Link] __REFERENCE__C_0402_1005Metric_null_ln_010  label="${REFERENCE}_C_0402_1005Metric_null011"
  LinkPlacement = pos=(106.045,-110.109,0) rot=(0,0,-1;1.5708rad)
  LinkedObject = -> Shape
  Placement = pos=(106.045,-110.109,0) rot=(0,0,-1;1.5708rad)
FEATURE [App::Link] __REFERENCE__R_0402_1005Metric_null_ln_010  label="${REFERENCE}_R_0402_1005Metric_null011"
  LinkPlacement = pos=(147.828,-91.821,0) rot=(0,0,-1;1.5708rad)
  LinkedObject = -> Shape003
  Placement = pos=(147.828,-91.821,0) rot=(0,0,-1;1.5708rad)
FEATURE [App::Link] __REFERENCE__LED_0603_1608Metric_null_ln_007  label="${REFERENCE}_LED_0603_1608Metric_null008"
  LinkPlacement = pos=(94.361,-89.408,0) rot=(0,0,1;0rad)
  LinkedObject = -> Shape005
  Placement = pos=(94.361,-89.408,0) rot=(0,0,1;0rad)
FEATURE [App::Link] __REFERENCE__C_0402_1005Metric_null_ln_011  label="${REFERENCE}_C_0402_1005Metric_null012"
  LinkPlacement = pos=(105.156,-112.141,0) rot=(0,0,-1;1.5708rad)
  LinkedObject = -> Shape
  Placement = pos=(105.156,-112.141,0) rot=(0,0,-1;1.5708rad)
FEATURE [App::Link] __REFERENCE__R_0603_1608Metric_null_ln_003  label="${REFERENCE}_R_0603_1608Metric_null004"
  LinkPlacement = pos=(122.809,-93.853,0) rot=(0,0,1;1.5708rad)
  LinkedObject = -> Shape002
  Placement = pos=(122.809,-93.853,0) rot=(0,0,1;1.5708rad)
FEATURE [App::Part] Top_31ac
  Group = -> [Shape,Shape001,Shape002,__REFERENCE__R_0603_1608Metric_null_ln_,Shape003,__REFERENCE__C_0402_1005Metric_null_ln_,__REFERENCE__R_0402_1005Metric_null_ln_,__REFERENCE__R_0402_1005Metric_null_ln_001,Shape004,__REFERENCE__R_0402_1005Metric_null_ln_002,__REFERENCE__C_0402_1005Metric_null_ln_001,__REFERENCE__R_0402_1005Metric_null_ln_003,Shape005,__REFERENCE__C_0402_1005Metric_null_ln_002,Shape006,+35 more]
  Origin = -> Origin003
FEATURE [App::Part] Step_Models_31ac
  Group = -> [Top_31ac]
  Origin = -> Origin002
FEATURE [Part::Feature] Shape012  label="topTracks_31ac"
  Placement = pos=(0,0,0.01) rot=(0,0,1;0rad)
  shape: bbox 56.49 x 64.3 x 2e-07 mm, 71 faces, 0 solids (baked)
FEATURE [Part::Feature] zones_area001  label="topZones_31ac"
  Placement = pos=(0,0,0.01) rot=(0,0,1;0rad)
  shape: bbox 103.5 x 118.6 x 2e-07 mm, 4 faces, 0 solids (baked)
FEATURE [Part::Feature] topPads_31ac_  label="topPads_31ac_cut"
  Placement = pos=(0,0,0.02) rot=(0,0,1;0rad)
  shape: bbox 59.65 x 67.91 x 2e-07 mm, 231 faces, 0 solids (baked)
FEATURE [Part::Feature] pads_area003  label="botPads_31ac"
  Placement = pos=(0,0,-1.62) rot=(0,0,1;0rad)
  shape: bbox 49.93 x 61.28 x 2e-07 mm, 42 faces, 0 solids (baked)
FEATURE [Part::Feature] Shape014  label="botTracks_31ac"
  Placement = pos=(0,0,-1.61) rot=(0,0,1;0rad)
  shape: bbox 49.41 x 60.55 x 2e-07 mm, 14 faces, 0 solids (baked)
FEATURE [Part::Feature] zones_area003  label="botZones_31ac"
  Placement = pos=(0,0,-1.61) rot=(0,0,1;0rad)
  shape: bbox 103.5 x 118.6 x 2e-07 mm, 1 faces, 0 solids (baked)
FEATURE [Part::Feature] topSilks_5558
  Placement = pos=(0,0,0.07) rot=(0,0,1;0rad)
  shape: bbox 60.47 x 68.9 x 2e-07 mm, 118 faces, 0 solids (baked)
FEATURE [Part::Feature] botSilks_588c
  Placement = pos=(0,0,-1.67) rot=(0,0,1;0rad)
  shape: bbox 66.34 x 74.54 x 2e-07 mm, 13 faces, 0 solids (baked)
FEATURE [App::Part] Board_Geoms_31ac
  Group = -> [Pcb_31ac,PCB_Sketch_31ac,topPads_31ac_,Shape012,zones_area001,pads_area003,Shape014,zones_area003,topSilks_5558,botSilks_588c]
  Origin = -> Origin
FEATURE [App::Part] Board_31ac  label="nerf-target-v1"
  Group = -> [Local_CS_31ac,Board_Geoms_31ac,Step_Models_31ac]
  Origin = -> Origin001
